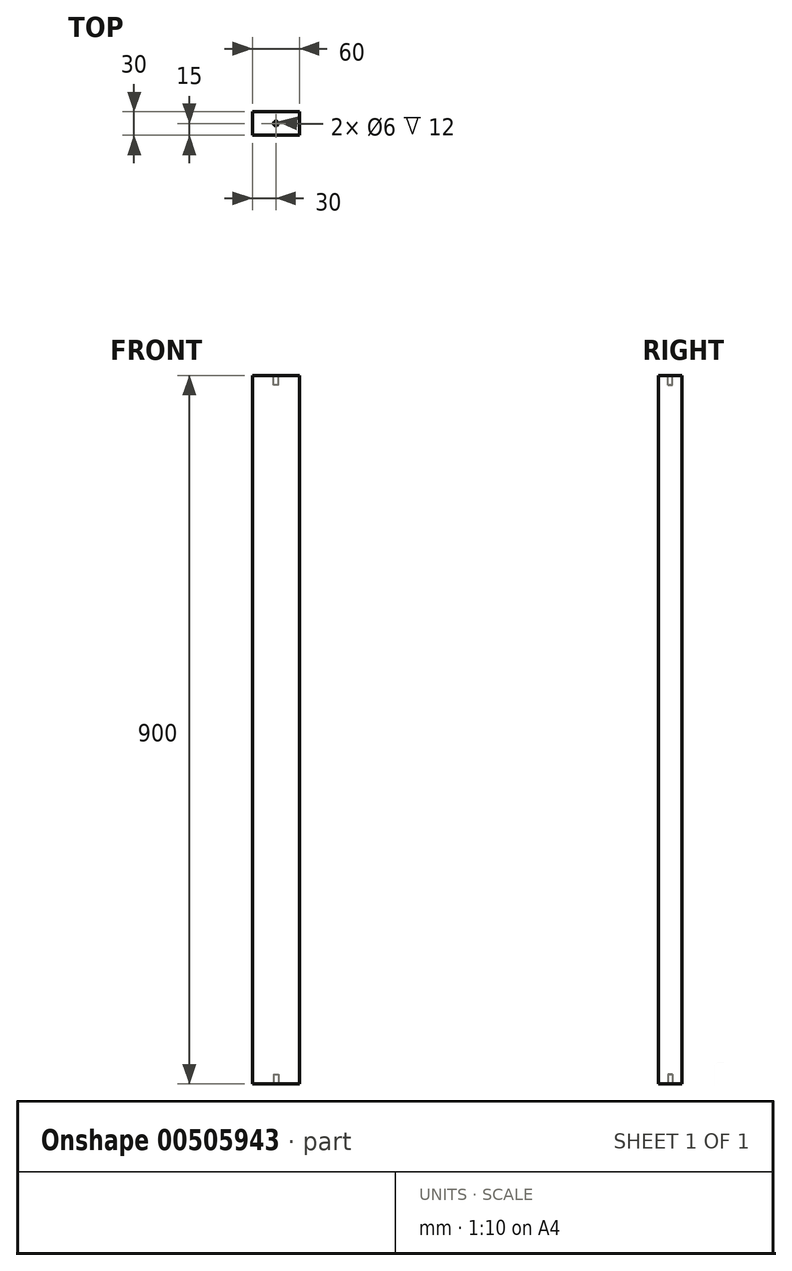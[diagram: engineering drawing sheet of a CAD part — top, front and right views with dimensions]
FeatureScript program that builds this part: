
annotation { "Feature Type Name" : "Feature", "Feature Type Description" : "" }
export const myFeature = defineFeature(function(context is Context, id is Id, definition is map)
    precondition{}
    {
        {
            var Q0;
            Q0=qCreatedBy(makeId("Top.planeOp"),FACE);
            var sketch = newSketch(context, id + "F0", { "sketchPlane" : qUnion([Q0])});
            skLineSegment(sketch, "E0.bottom", {"start": v(0, 0) * mm, "end": v(60, 0) * mm});
            skLineSegment(sketch, "E0.top", {"start": v(0, 30) * mm, "end": v(60, 30) * mm});
            skLineSegment(sketch, "E0.left", {"start": v(0, 0) * mm, "end": v(0, 30) * mm});
            skLineSegment(sketch, "E0.right", {"start": v(60, 0) * mm, "end": v(60, 30) * mm});
            skSolve(sketch);
        }
        {
            var Q0;
            Q0=makeQuery(id+"F0.imprint","IMPRINT",FACE,{"disambiguationData":[TD([[makeQuery(id+"F0.imprint","IMPRINT",EDGE,{"derivedFrom":sQuery(id+"F0.wireOp",EDGE,"E0.bottom")}),1.0]])]});
            extrude(context, id + "F1", {"entities" : qUnion([Q0]), "depth" : 900 * mm, "offsetDistance" : 25 * mm});
        }
        {
            var Q0;
            Q0=makeQuery(id+"F1.opExtrude","CAP_FACE",FACE,{"disambiguationData":[OSD([sQuery(id+"F0.wireOp",EDGE,"E0.bottom"),sQuery(id+"F0.wireOp",EDGE,"E0.top"),sQuery(id+"F0.wireOp",EDGE,"E0.left"),sQuery(id+"F0.wireOp",EDGE,"E0.right")])],"isStart":false});
            var sketch = newSketch(context, id + "F2", { "sketchPlane" : qUnion([Q0])});
            skSolve(sketch);
        }
        {
            var Q0;
            Q0=makeQuery(id+"F2.imprint","IMPRINT",FACE,{"disambiguationData":[TD([[makeQuery(id+"F2.imprint","IMPRINT",EDGE,{"derivedFrom":makeQuery(id+"F1.opExtrude","CAP_EDGE",EDGE,{"disambiguationData":[OSD([sQuery(id+"F0.wireOp",EDGE,"E0.bottom")])],"isStart":false})}),1.0]])]});
            var sketch = newSketch(context, id + "F3", { "sketchPlane" : qUnion([Q0])});
            skCircle(sketch, "E1", {"center": v(30, 15) * mm, "radius": 3 * mm});
            skSolve(sketch);
        }
        {
            var Q0;
            Q0 = qSketchRegion(id + "F3", true);
            extrude(context, id + "F4", {"entities" : qUnion([Q0]), "operationType" : NewBodyOperationType.REMOVE, "oppositeDirection" : true, "depth" : 12 * mm, "offsetDistance" : 25 * mm});
        }
        {
            var Q0;
            Q0=makeQuery(id+"F1.opExtrude","CAP_FACE",FACE,{"disambiguationData":[OSD([sQuery(id+"F0.wireOp",EDGE,"E0.bottom"),sQuery(id+"F0.wireOp",EDGE,"E0.top"),sQuery(id+"F0.wireOp",EDGE,"E0.left"),sQuery(id+"F0.wireOp",EDGE,"E0.right")])],"isStart":true});
            var sketch = newSketch(context, id + "F5", { "sketchPlane" : qUnion([Q0])});
            skCircle(sketch, "E2", {"center": v(30, -15) * mm, "radius": 3 * mm});
            skSolve(sketch);
        }
        {
            var Q0;
            Q0=makeQuery(id+"F5.imprint","IMPRINT",FACE,{"disambiguationData":[TD([[makeQuery(id+"F5.imprint","IMPRINT",EDGE,{"derivedFrom":sQuery(id+"F5.wireOp",EDGE,"E2")}),1.0]])]});
            extrude(context, id + "F6", {"entities" : qUnion([Q0]), "operationType" : NewBodyOperationType.REMOVE, "oppositeDirection" : true, "depth" : 12 * mm, "offsetDistance" : 25 * mm});
        }
    });
